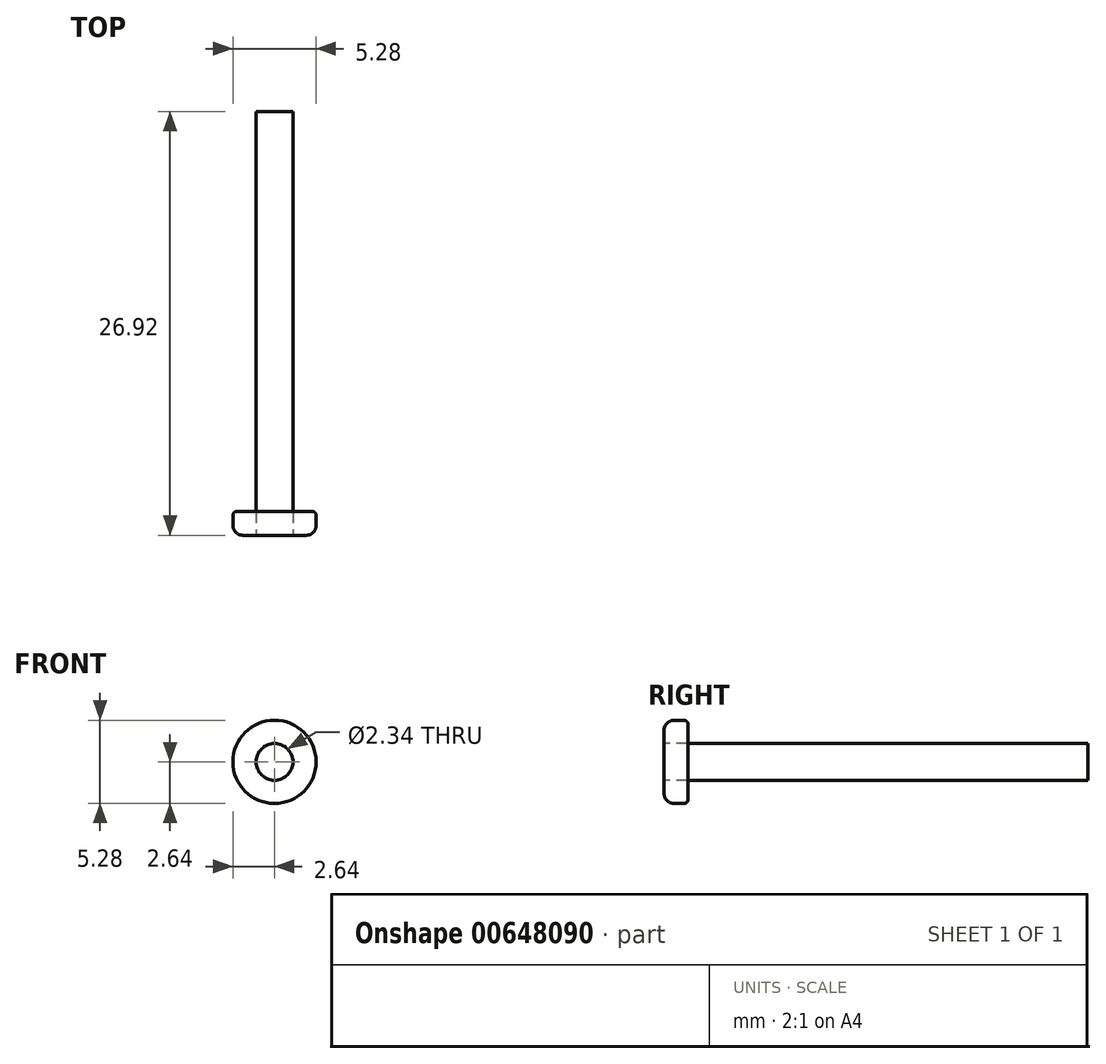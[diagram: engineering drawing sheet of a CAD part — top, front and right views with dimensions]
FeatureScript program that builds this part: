
annotation { "Feature Type Name" : "Feature", "Feature Type Description" : "" }
export const myFeature = defineFeature(function(context is Context, id is Id, definition is map)
    precondition{}
    {
        {
            var Q0;
            Q0=qCreatedBy(makeId("Front.planeOp"),FACE);
            var sketch = newSketch(context, id + "F0", { "sketchPlane" : qUnion([Q0])});
            skCircle(sketch, "E0", {"center": v(0, 0) * mm, "radius": 2.64 * mm});
            skCircle(sketch, "E1", {"center": v(0, 0) * mm, "radius": 1.17 * mm});
            skSolve(sketch);
        }
        {
            var Q0;
            Q0=makeQuery(id+"F0.imprint","IMPRINT",FACE,{"disambiguationData":[TD([[makeQuery(id+"F0.imprint","IMPRINT",EDGE,{"derivedFrom":sQuery(id+"F0.wireOp",EDGE,"E0")}),1.0]])]});
            extrude(context, id + "F1", {"entities" : qUnion([Q0]), "oppositeDirection" : true, "depth" : 1.52 * mm, "offsetDistance" : 25.4 * mm});
        }
        {
            var Q0;
            Q0=makeQuery(id+"F1.opExtrude","CAP_FACE",FACE,{"disambiguationData":[OSD([sQuery(id+"F0.wireOp",EDGE,"E0"),sQuery(id+"F0.wireOp",EDGE,"E1")])],"isStart":true});
            var sketch = newSketch(context, id + "F2", { "sketchPlane" : qUnion([Q0])});
            skCircle(sketch, "E2", {"center": v(0, 0) * mm, "radius": 1.17 * mm});
            skSolve(sketch);
        }
        {
            var Q0;
            Q0=makeQuery(id+"F2.imprint","IMPRINT",FACE,{"disambiguationData":[TD([[makeQuery(id+"F2.imprint","IMPRINT",EDGE,{"derivedFrom":sQuery(id+"F2.wireOp",EDGE,"E2")}),1.0]])]});
            extrude(context, id + "F3", {"entities" : qUnion([Q0]), "oppositeDirection" : true, "depth" : 26.92 * mm, "offsetDistance" : 25.4 * mm});
        }
        {
            var Q0;
            Q0=makeQuery(id+"F1.opExtrude","CAP_EDGE",EDGE,{"disambiguationData":[OSD([sQuery(id+"F0.wireOp",EDGE,"E0")])],"isStart":true});
            fillet(context, id + "F4", {"entities" : qUnion([Q0]), "radius" : 0.64 * mm, "tangentPropagation" : true, "allowEdgeOverflow" : false});
        }
        {
            var Q0;
            Q0=makeQuery(id+"F1.opExtrude","CAP_EDGE",EDGE,{"disambiguationData":[OSD([sQuery(id+"F0.wireOp",EDGE,"E0")])],"isStart":false});
            fillet(context, id + "F5", {"entities" : qUnion([Q0]), "radius" : 0.25 * mm, "tangentPropagation" : true, "allowEdgeOverflow" : false});
        }
    });
